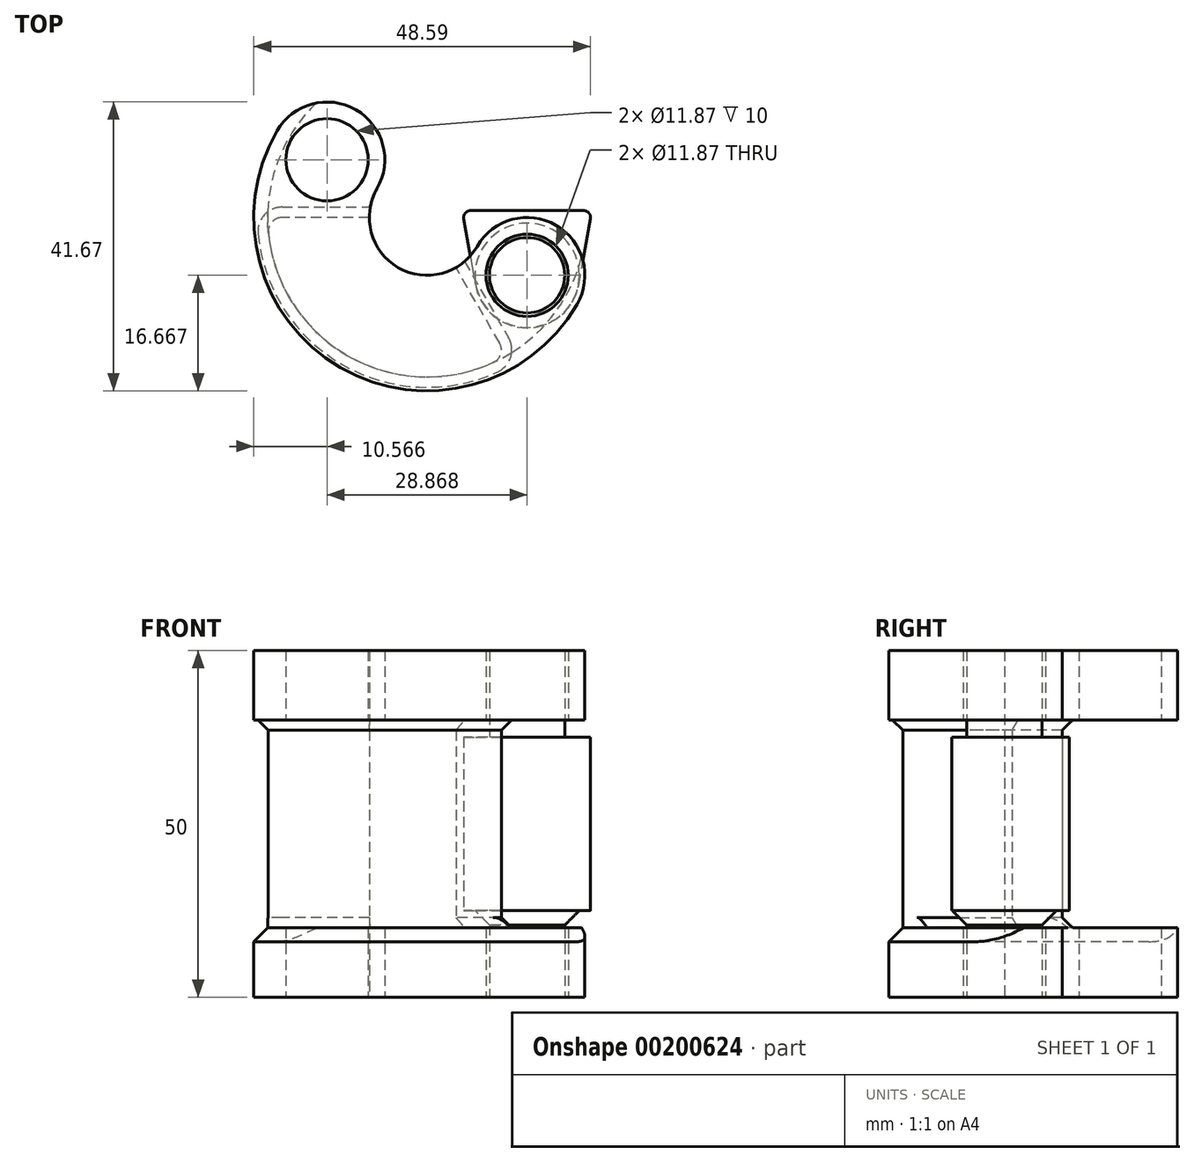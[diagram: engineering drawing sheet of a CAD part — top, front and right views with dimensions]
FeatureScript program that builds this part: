
annotation { "Feature Type Name" : "Feature", "Feature Type Description" : "" }
export const myFeature = defineFeature(function(context is Context, id is Id, definition is map)
    precondition{}
    {
        {
            assignVariable(context, id + "F0", {"name" : "height", "anyValue" : 50});
        }
        {
            var Q0;
            Q0=qCreatedBy(makeId("Top.planeOp"),FACE);
            var sketch = newSketch(context, id + "F1", { "sketchPlane" : qUnion([Q0])});
            skCircle(sketch, "E0", {"center": v(0, 0) * mm, "radius": 25 * mm});
            skLineSegment(sketch, "E1", {"start": v(25, 0) * mm, "end": v(0, 0) * mm});
            skLineSegment(sketch, "E2", {"start": v(0, 0) * mm, "end": v(-12.5, 21.65) * mm});
            skCircle(sketch, "E3", {"center": v(0, 0) * mm, "radius": 8.33 * mm});
            skCircle(sketch, "E4", {"center": v(0, 0) * mm, "radius": 23 * mm});
            skCircle(sketch, "E5", {"center": v(-14.43, 8.33) * mm, "radius": 8.33 * mm});
            skCircle(sketch, "E6", {"center": v(14.43, -8.33) * mm, "radius": 8.33 * mm});
            skCircle(sketch, "E7", {"center": v(-14.43, 8.33) * mm, "radius": 5.93 * mm});
            skCircle(sketch, "E8", {"center": v(14.43, -8.33) * mm, "radius": 5.93 * mm});
            skLineSegment(sketch, "E9", {"start": v(4.17, -7.22) * mm, "end": v(12.5, -21.65) * mm});
            skLineSegment(sketch, "E10", {"start": v(-8.33, 0) * mm, "end": v(-25, 0) * mm});
            skSolve(sketch);
        }
        {
            var Q0;
            {var subQ0=sQuery(id+"F1.wireOp",EDGE,"E5");var subQ1=sQuery(id+"F1.wireOp",EDGE,"E3");var subQ2=makeQuery(id+"F1.imprint","INTERSECT",VERTEX,{"derivedFrom":[subQ1,subQ0]});Q0=makeQuery(id+"F1.imprint","IMPRINT",FACE,{"disambiguationData":[TD([[makeQuery(id+"F1.imprint","IMPRINT",EDGE,{"disambiguationData":[TD([[subQ2,-1.0]])],"derivedFrom":subQ1}),-1.0]])]});}
            var Q1;
            {var subQ0=sQuery(id+"F1.wireOp",EDGE,"E5");var subQ1=sQuery(id+"F1.wireOp",EDGE,"E4");var subQ2=makeQuery(id+"F1.imprint","INTERSECT",VERTEX,{"disambiguationData":[OD(0.0)],"derivedFrom":[subQ1,subQ0]});Q1=makeQuery(id+"F1.imprint","IMPRINT",FACE,{"disambiguationData":[TD([[makeQuery(id+"F1.imprint","IMPRINT",EDGE,{"disambiguationData":[TD([[subQ2,-1.0]])],"derivedFrom":subQ1}),1.0]])]});}
            var Q2;
            {var subQ0=sQuery(id+"F1.wireOp",EDGE,"E6");var subQ1=sQuery(id+"F1.wireOp",EDGE,"E4");var subQ2=makeQuery(id+"F1.imprint","INTERSECT",VERTEX,{"disambiguationData":[OD(0.0)],"derivedFrom":[subQ1,subQ0]});Q2=makeQuery(id+"F1.imprint","IMPRINT",FACE,{"disambiguationData":[TD([[makeQuery(id+"F1.imprint","IMPRINT",EDGE,{"disambiguationData":[TD([[subQ2,-1.0]])],"derivedFrom":subQ1}),1.0]])]});}
            var Q3;
            {var subQ0=sQuery(id+"F1.wireOp",EDGE,"E5");var subQ1=sQuery(id+"F1.wireOp",EDGE,"E0");var subQ2=makeQuery(id+"F1.imprint","INTERSECT",VERTEX,{"derivedFrom":[subQ1,subQ0]});Q3=makeQuery(id+"F1.imprint","IMPRINT",FACE,{"disambiguationData":[TD([[makeQuery(id+"F1.imprint","IMPRINT",EDGE,{"disambiguationData":[TD([[subQ2,-1.0]])],"derivedFrom":subQ1}),1.0]])]});}
            var Q4;
            {var subQ0=sQuery(id+"F1.wireOp",EDGE,"E5");var subQ1=sQuery(id+"F1.wireOp",EDGE,"E4");var subQ2=makeQuery(id+"F1.imprint","INTERSECT",VERTEX,{"disambiguationData":[OD(0.0)],"derivedFrom":[subQ1,subQ0]});Q4=makeQuery(id+"F1.imprint","IMPRINT",FACE,{"disambiguationData":[TD([[makeQuery(id+"F1.imprint","IMPRINT",EDGE,{"disambiguationData":[TD([[subQ2,-1.0]])],"derivedFrom":subQ1}),-1.0]])]});}
            var Q5;
            {var subQ0=sQuery(id+"F1.wireOp",EDGE,"E6");var subQ1=sQuery(id+"F1.wireOp",EDGE,"E4");var subQ2=makeQuery(id+"F1.imprint","INTERSECT",VERTEX,{"disambiguationData":[OD(0.0)],"derivedFrom":[subQ1,subQ0]});Q5=makeQuery(id+"F1.imprint","IMPRINT",FACE,{"disambiguationData":[TD([[makeQuery(id+"F1.imprint","IMPRINT",EDGE,{"disambiguationData":[TD([[subQ2,-1.0]])],"derivedFrom":subQ1}),-1.0]])]});}
            var Q6;
            {var subQ0=sQuery(id+"F1.wireOp",EDGE,"E5");var subQ1=sQuery(id+"F1.wireOp",EDGE,"E4");var subQ2=makeQuery(id+"F1.imprint","INTERSECT",VERTEX,{"disambiguationData":[OD(1.0)],"derivedFrom":[subQ1,subQ0]});Q6=makeQuery(id+"F1.imprint","IMPRINT",FACE,{"disambiguationData":[TD([[makeQuery(id+"F1.imprint","IMPRINT",EDGE,{"disambiguationData":[TD([[subQ2,-1.0]])],"derivedFrom":subQ1}),1.0]])]});}
            var Q7;
            {var subQ0=sQuery(id+"F1.wireOp",EDGE,"E9");var subQ4=sQuery(id+"F1.wireOp",EDGE,"E3");var subQ5=makeQuery(id+"F1.imprint","INTERSECT",VERTEX,{"derivedFrom":[subQ4,subQ0]});Q7=makeQuery(id+"F1.imprint","IMPRINT",FACE,{"disambiguationData":[TD([[makeQuery(id+"F1.imprint","IMPRINT",EDGE,{"disambiguationData":[TD([[subQ5,1.0]])],"derivedFrom":subQ4}),-1.0]])]});}
            var Q8;
            {var subQ0=sQuery(id+"F1.wireOp",EDGE,"E9");var subQ1=sQuery(id+"F1.wireOp",EDGE,"E0");var subQ2=makeQuery(id+"F1.imprint","INTERSECT",VERTEX,{"derivedFrom":[subQ1,subQ0]});Q8=makeQuery(id+"F1.imprint","IMPRINT",FACE,{"disambiguationData":[TD([[makeQuery(id+"F1.imprint","IMPRINT",EDGE,{"disambiguationData":[TD([[subQ2,1.0]])],"derivedFrom":subQ1}),1.0]])]});}
            var Q9;
            {var subQ0=sQuery(id+"F1.wireOp",EDGE,"E9");var subQ1=sQuery(id+"F1.wireOp",EDGE,"E3");var subQ2=makeQuery(id+"F1.imprint","INTERSECT",VERTEX,{"derivedFrom":[subQ1,subQ0]});Q9=makeQuery(id+"F1.imprint","IMPRINT",FACE,{"disambiguationData":[TD([[makeQuery(id+"F1.imprint","IMPRINT",EDGE,{"disambiguationData":[TD([[subQ2,-1.0]])],"derivedFrom":subQ1}),-1.0]])]});}
            var Q10;
            {var subQ0=sQuery(id+"F1.wireOp",EDGE,"E9");var subQ1=sQuery(id+"F1.wireOp",EDGE,"E4");var subQ2=makeQuery(id+"F1.imprint","INTERSECT",VERTEX,{"derivedFrom":[subQ1,subQ0]});Q10=makeQuery(id+"F1.imprint","IMPRINT",FACE,{"disambiguationData":[TD([[makeQuery(id+"F1.imprint","IMPRINT",EDGE,{"disambiguationData":[TD([[subQ2,-1.0]])],"derivedFrom":subQ1}),1.0]])]});}
            var Q11;
            {var subQ0=sQuery(id+"F1.wireOp",EDGE,"E9");var subQ1=sQuery(id+"F1.wireOp",EDGE,"E0");var subQ2=makeQuery(id+"F1.imprint","INTERSECT",VERTEX,{"derivedFrom":[subQ1,subQ0]});Q11=makeQuery(id+"F1.imprint","IMPRINT",FACE,{"disambiguationData":[TD([[makeQuery(id+"F1.imprint","IMPRINT",EDGE,{"disambiguationData":[TD([[subQ2,-1.0]])],"derivedFrom":subQ1}),1.0]])]});}
            extrude(context, id + "F2", {"entities" : qUnion([Q0, Q1, Q2, Q3, Q4, Q5, Q6, Q7, Q8, Q9, Q10, Q11]), "endBound" : BoundingType.SYMMETRIC, "depth" : (getVariable(context, 'height')) * mm});
        }
        {
            var Q0;
            {var subQ0=sQuery(id+"F1.wireOp",EDGE,"E5");var subQ1=sQuery(id+"F1.wireOp",EDGE,"E0");var subQ2=makeQuery(id+"F1.imprint","INTERSECT",VERTEX,{"derivedFrom":[subQ1,subQ0]});Q0=makeQuery(id+"F1.imprint","IMPRINT",FACE,{"disambiguationData":[TD([[makeQuery(id+"F1.imprint","IMPRINT",EDGE,{"disambiguationData":[TD([[subQ2,-1.0]])],"derivedFrom":subQ1}),1.0]])]});}
            var Q1;
            {var subQ0=sQuery(id+"F1.wireOp",EDGE,"E5");var subQ1=sQuery(id+"F1.wireOp",EDGE,"E4");var subQ2=makeQuery(id+"F1.imprint","INTERSECT",VERTEX,{"disambiguationData":[OD(0.0)],"derivedFrom":[subQ1,subQ0]});Q1=makeQuery(id+"F1.imprint","IMPRINT",FACE,{"disambiguationData":[TD([[makeQuery(id+"F1.imprint","IMPRINT",EDGE,{"disambiguationData":[TD([[subQ2,-1.0]])],"derivedFrom":subQ1}),-1.0]])]});}
            var Q2;
            {var subQ0=sQuery(id+"F1.wireOp",EDGE,"E6");var subQ1=sQuery(id+"F1.wireOp",EDGE,"E4");var subQ2=makeQuery(id+"F1.imprint","INTERSECT",VERTEX,{"disambiguationData":[OD(0.0)],"derivedFrom":[subQ1,subQ0]});Q2=makeQuery(id+"F1.imprint","IMPRINT",FACE,{"disambiguationData":[TD([[makeQuery(id+"F1.imprint","IMPRINT",EDGE,{"disambiguationData":[TD([[subQ2,-1.0]])],"derivedFrom":subQ1}),-1.0]])]});}
            var Q3;
            {var subQ0=sQuery(id+"F1.wireOp",EDGE,"E9");var subQ1=sQuery(id+"F1.wireOp",EDGE,"E0");var subQ2=makeQuery(id+"F1.imprint","INTERSECT",VERTEX,{"derivedFrom":[subQ1,subQ0]});Q3=makeQuery(id+"F1.imprint","IMPRINT",FACE,{"disambiguationData":[TD([[makeQuery(id+"F1.imprint","IMPRINT",EDGE,{"disambiguationData":[TD([[subQ2,1.0]])],"derivedFrom":subQ1}),1.0]])]});}
            var Q4;
            {var subQ0=sQuery(id+"F1.wireOp",EDGE,"E9");var subQ1=sQuery(id+"F1.wireOp",EDGE,"E0");var subQ2=makeQuery(id+"F1.imprint","INTERSECT",VERTEX,{"derivedFrom":[subQ1,subQ0]});Q4=makeQuery(id+"F1.imprint","IMPRINT",FACE,{"disambiguationData":[TD([[makeQuery(id+"F1.imprint","IMPRINT",EDGE,{"disambiguationData":[TD([[subQ2,-1.0]])],"derivedFrom":subQ1}),1.0]])]});}
            extrude(context, id + "F3", {"entities" : qUnion([Q0, Q1, Q2, Q3, Q4]), "operationType" : NewBodyOperationType.REMOVE, "endBound" : BoundingType.SYMMETRIC, "oppositeDirection" : true, "depth" : 30 * mm});
        }
        {
            var Q0;
            Q0=makeQuery(id+"F1.imprint","IMPRINT",FACE,{"disambiguationData":[TD([[makeQuery(id+"F1.imprint","IMPRINT",EDGE,{"derivedFrom":sQuery(id+"F1.wireOp",EDGE,"E7")}),-1.0]])]});
            var Q1;
            Q1=makeQuery(id+"F1.imprint","IMPRINT",FACE,{"disambiguationData":[TD([[makeQuery(id+"F1.imprint","IMPRINT",EDGE,{"derivedFrom":sQuery(id+"F1.wireOp",EDGE,"E7")}),1.0]])]});
            var Q2;
            {var subQ0=sQuery(id+"F1.wireOp",EDGE,"E5");var subQ1=sQuery(id+"F1.wireOp",EDGE,"E4");var subQ2=makeQuery(id+"F1.imprint","INTERSECT",VERTEX,{"disambiguationData":[OD(0.0)],"derivedFrom":[subQ1,subQ0]});Q2=makeQuery(id+"F1.imprint","IMPRINT",FACE,{"disambiguationData":[TD([[makeQuery(id+"F1.imprint","IMPRINT",EDGE,{"disambiguationData":[TD([[subQ2,-1.0]])],"derivedFrom":subQ1}),-1.0]])]});}
            var Q3;
            Q3=makeQuery(id+"F1.imprint","IMPRINT",FACE,{"disambiguationData":[TD([[makeQuery(id+"F1.imprint","IMPRINT",EDGE,{"derivedFrom":sQuery(id+"F1.wireOp",EDGE,"E8")}),-1.0]])]});
            var Q4;
            Q4=makeQuery(id+"F1.imprint","IMPRINT",FACE,{"disambiguationData":[TD([[makeQuery(id+"F1.imprint","IMPRINT",EDGE,{"derivedFrom":sQuery(id+"F1.wireOp",EDGE,"E8")}),1.0]])]});
            var Q5;
            {var subQ0=sQuery(id+"F1.wireOp",EDGE,"E6");var subQ1=sQuery(id+"F1.wireOp",EDGE,"E4");var subQ2=makeQuery(id+"F1.imprint","INTERSECT",VERTEX,{"disambiguationData":[OD(0.0)],"derivedFrom":[subQ1,subQ0]});Q5=makeQuery(id+"F1.imprint","IMPRINT",FACE,{"disambiguationData":[TD([[makeQuery(id+"F1.imprint","IMPRINT",EDGE,{"disambiguationData":[TD([[subQ2,-1.0]])],"derivedFrom":subQ1}),-1.0]])]});}
            var Q6;
            {var subQ0=sQuery(id+"F1.wireOp",EDGE,"E9");var subQ1=sQuery(id+"F1.wireOp",EDGE,"E0");var subQ2=makeQuery(id+"F1.imprint","INTERSECT",VERTEX,{"derivedFrom":[subQ1,subQ0]});Q6=makeQuery(id+"F1.imprint","IMPRINT",FACE,{"disambiguationData":[TD([[makeQuery(id+"F1.imprint","IMPRINT",EDGE,{"disambiguationData":[TD([[subQ2,-1.0]])],"derivedFrom":subQ1}),1.0]])]});}
            var Q7;
            {var subQ0=sQuery(id+"F1.wireOp",EDGE,"E9");var subQ1=sQuery(id+"F1.wireOp",EDGE,"E4");var subQ2=makeQuery(id+"F1.imprint","INTERSECT",VERTEX,{"derivedFrom":[subQ1,subQ0]});Q7=makeQuery(id+"F1.imprint","IMPRINT",FACE,{"disambiguationData":[TD([[makeQuery(id+"F1.imprint","IMPRINT",EDGE,{"disambiguationData":[TD([[subQ2,-1.0]])],"derivedFrom":subQ1}),1.0]])]});}
            var Q8;
            {var subQ0=sQuery(id+"F1.wireOp",EDGE,"E9");var subQ1=sQuery(id+"F1.wireOp",EDGE,"E3");var subQ2=makeQuery(id+"F1.imprint","INTERSECT",VERTEX,{"derivedFrom":[subQ1,subQ0]});Q8=makeQuery(id+"F1.imprint","IMPRINT",FACE,{"disambiguationData":[TD([[makeQuery(id+"F1.imprint","IMPRINT",EDGE,{"disambiguationData":[TD([[subQ2,-1.0]])],"derivedFrom":subQ1}),-1.0]])]});}
            var Q9;
            {var subQ0=sQuery(id+"F1.wireOp",EDGE,"E10");var subQ1=sQuery(id+"F1.wireOp",EDGE,"E3");var subQ2=makeQuery(id+"F1.imprint","INTERSECT",VERTEX,{"derivedFrom":[subQ1,subQ0]});Q9=makeQuery(id+"F1.imprint","IMPRINT",FACE,{"disambiguationData":[TD([[makeQuery(id+"F1.imprint","IMPRINT",EDGE,{"disambiguationData":[TD([[subQ2,1.0]])],"derivedFrom":subQ1}),-1.0]])]});}
            var Q10;
            {var subQ0=sQuery(id+"F1.wireOp",EDGE,"E5");var subQ1=sQuery(id+"F1.wireOp",EDGE,"E4");var subQ2=makeQuery(id+"F1.imprint","INTERSECT",VERTEX,{"disambiguationData":[OD(1.0)],"derivedFrom":[subQ1,subQ0]});Q10=makeQuery(id+"F1.imprint","IMPRINT",FACE,{"disambiguationData":[TD([[makeQuery(id+"F1.imprint","IMPRINT",EDGE,{"disambiguationData":[TD([[subQ2,-1.0]])],"derivedFrom":subQ1}),1.0]])]});}
            var Q11;
            {var subQ0=sQuery(id+"F1.wireOp",EDGE,"E10");var subQ1=sQuery(id+"F1.wireOp",EDGE,"E0");var subQ2=makeQuery(id+"F1.imprint","INTERSECT",VERTEX,{"derivedFrom":[subQ1,subQ0]});Q11=makeQuery(id+"F1.imprint","IMPRINT",FACE,{"disambiguationData":[TD([[makeQuery(id+"F1.imprint","IMPRINT",EDGE,{"disambiguationData":[TD([[subQ2,1.0]])],"derivedFrom":subQ1}),1.0]])]});}
            extrude(context, id + "F4", {"entities" : qUnion([Q0, Q1, Q2, Q3, Q4, Q5, Q6, Q7, Q8, Q9, Q10, Q11]), "operationType" : NewBodyOperationType.REMOVE, "endBound" : BoundingType.SYMMETRIC, "depth" : 30 * mm});
        }
        {
            var Q0;
            Q0=makeQuery(id+"F3.boolean.opBoolean","COPY",EDGE,{"derivedFrom":makeQuery(id+"F3.opExtrude","CAP_EDGE",EDGE,{"disambiguationData":[OSD([sQuery(id+"F1.wireOp",EDGE,"E0")])],"isStart":true})});
            var Q1;
            Q1=makeQuery(id+"F3.boolean.opBoolean","COPY",EDGE,{"derivedFrom":makeQuery(id+"F3.opExtrude","CAP_EDGE",EDGE,{"disambiguationData":[OSD([sQuery(id+"F1.wireOp",EDGE,"E0")])],"isStart":false})});
            chamfer(context, id + "F5", {"entities" : qUnion([Q0, Q1]), "width" : 2 * mm});
        }
        {
            var Q0;
            Q0=makeQuery(id+"F4.boolean.opBoolean","INTERSECT",EDGE,{"derivedFrom":[makeQuery(id+"F3.boolean.opBoolean","COPY",FACE,{"derivedFrom":makeQuery(id+"F3.opExtrude","SWEPT_FACE",FACE,{"disambiguationData":[OSD([sQuery(id+"F1.wireOp",EDGE,"E4")])]})}),makeQuery(id+"F4.opExtrude","SWEPT_FACE",FACE,{"disambiguationData":[OSD([sQuery(id+"F1.wireOp",EDGE,"E9")])]})]});
            var Q1;
            Q1=makeQuery(id+"F4.boolean.opBoolean","INTERSECT",EDGE,{"derivedFrom":[makeQuery(id+"F3.boolean.opBoolean","COPY",FACE,{"derivedFrom":makeQuery(id+"F3.opExtrude","SWEPT_FACE",FACE,{"disambiguationData":[OSD([sQuery(id+"F1.wireOp",EDGE,"E4")])]})}),makeQuery(id+"F4.opExtrude","SWEPT_FACE",FACE,{"disambiguationData":[OSD([sQuery(id+"F1.wireOp",EDGE,"E10")])]})]});
            var Q2;
            Q2=makeQuery(id+"F4.boolean.opBoolean","INTERSECT",EDGE,{"derivedFrom":[makeQuery(id+"F3.boolean.opBoolean","COPY",FACE,{"derivedFrom":makeQuery(id+"F3.opExtrude","SWEPT_FACE",FACE,{"disambiguationData":[OSD([sQuery(id+"F1.wireOp",EDGE,"E4")])]})}),makeQuery(id+"F4.opExtrude","SWEPT_FACE",FACE,{"disambiguationData":[OSD([sQuery(id+"F1.wireOp",EDGE,"E9")])]})]});
            var Q3;
            Q3=makeQuery(id+"F4.boolean.opBoolean","INTERSECT",EDGE,{"derivedFrom":[makeQuery(id+"F3.boolean.opBoolean","COPY",FACE,{"derivedFrom":makeQuery(id+"F3.opExtrude","SWEPT_FACE",FACE,{"disambiguationData":[OSD([sQuery(id+"F1.wireOp",EDGE,"E4")])]})}),makeQuery(id+"F4.opExtrude","SWEPT_FACE",FACE,{"disambiguationData":[OSD([sQuery(id+"F1.wireOp",EDGE,"E10")])]})]});
            var Q4;
            Q4=makeQuery(id+"F4.boolean.opBoolean","COPY",EDGE,{"derivedFrom":makeQuery(id+"F4.opExtrude","SWEPT_EDGE",EDGE,{"disambiguationData":[OSD([sQuery(id+"F1.wireOp",EDGE,"E3"),sQuery(id+"F1.wireOp",EDGE,"E9")])]})});
            var Q5;
            Q5=makeQuery(id+"F4.boolean.opBoolean","COPY",EDGE,{"derivedFrom":makeQuery(id+"F4.opExtrude","SWEPT_EDGE",EDGE,{"disambiguationData":[OSD([sQuery(id+"F1.wireOp",EDGE,"E3"),sQuery(id+"F1.wireOp",EDGE,"E10")])]})});
            fillet(context, id + "F6", {"entities" : qUnion([Q0, Q1, Q2, Q3, Q4, Q5]), "radius" : 2 * mm, "tangentPropagation" : true, "allowEdgeOverflow" : false});
        }
        {
            var Q0;
            Q0=makeQuery(id+"F4.boolean.opBoolean","COPY",EDGE,{"derivedFrom":makeQuery(id+"F4.opExtrude","CAP_EDGE",EDGE,{"disambiguationData":[OSD([sQuery(id+"F1.wireOp",EDGE,"E9")])],"isStart":false})});
            var Q1;
            Q1=makeQuery(id+"F4.boolean.opBoolean","COPY",EDGE,{"derivedFrom":makeQuery(id+"F4.opExtrude","CAP_EDGE",EDGE,{"disambiguationData":[OSD([sQuery(id+"F1.wireOp",EDGE,"E10")])],"isStart":false})});
            var Q2;
            Q2=makeQuery(id+"F4.boolean.opBoolean","COPY",EDGE,{"derivedFrom":makeQuery(id+"F4.opExtrude","CAP_EDGE",EDGE,{"disambiguationData":[OSD([sQuery(id+"F1.wireOp",EDGE,"E10")])],"isStart":true})});
            var Q3;
            Q3=makeQuery(id+"F4.boolean.opBoolean","COPY",EDGE,{"derivedFrom":makeQuery(id+"F4.opExtrude","CAP_EDGE",EDGE,{"disambiguationData":[OSD([sQuery(id+"F1.wireOp",EDGE,"E9")])],"isStart":true})});
            chamfer(context, id + "F7", {"entities" : qUnion([Q0, Q1, Q2, Q3]), "width" : 1.5 * mm, "tangentPropagation" : true});
        }
        {
            var Q0;
            Q0=qCreatedBy(makeId("Top.planeOp"),FACE);
            var sketch = newSketch(context, id + "F8", { "sketchPlane" : qUnion([Q0])});
            skCircle(sketch, "E11.0", {"center": v(14.43, -8.33) * mm, "radius": 5.93 * mm, "construction": true});
            skCircle(sketch, "E12", {"center": v(14.43, -8.33) * mm, "radius": 5.43 * mm});
            skCircle(sketch, "E13.0", {"center": v(14.43, -8.33) * mm, "radius": 8.33 * mm, "construction": true});
            skCircle(sketch, "E14", {"center": v(14.43, -8.33) * mm, "radius": 7.58 * mm});
            skLineSegment(sketch, "E15", {"start": v(21.9, -9.65) * mm, "end": v(23.78, 1) * mm});
            skLineSegment(sketch, "E16", {"start": v(23.78, 1) * mm, "end": v(5.09, 1) * mm});
            skLineSegment(sketch, "E17", {"start": v(5.09, 1) * mm, "end": v(6.97, -9.65) * mm});
            skSolve(sketch);
        }
        {
            var Q0;
            Q0=makeQuery(id+"F8.imprint","IMPRINT",FACE,{"disambiguationData":[TD([[makeQuery(id+"F8.imprint","IMPRINT",EDGE,{"derivedFrom":sQuery(id+"F8.wireOp",EDGE,"E12")}),1.0]])]});
            extrude(context, id + "F9", {"entities" : qUnion([Q0]), "endBound" : BoundingType.SYMMETRIC, "depth" : (getVariable(context, 'height')) * mm});
        }
        {
            var Q0;
            Q0=makeQuery(id+"F8.imprint","IMPRINT",FACE,{"disambiguationData":[TD([[makeQuery(id+"F8.imprint","IMPRINT",EDGE,{"derivedFrom":sQuery(id+"F8.wireOp",EDGE,"E12")}),-1.0]])]});
            var Q1;
            {var subQ0=sQuery(id+"F8.wireOp",EDGE,"E15");Q1=makeQuery(id+"F8.imprint","IMPRINT",FACE,{"disambiguationData":[TD([[makeQuery(id+"F8.imprint","IMPRINT",EDGE,{"derivedFrom":subQ0}),1.0]])]});}
            extrude(context, id + "F10", {"entities" : qUnion([Q0, Q1]), "operationType" : NewBodyOperationType.ADD, "endBound" : BoundingType.SYMMETRIC, "depth" : 25 * mm});
        }
        {
            var Q0;
            Q0=makeQuery(id+"F10.opExtrude","CAP_EDGE",EDGE,{"disambiguationData":[OSD([sQuery(id+"F8.wireOp",EDGE,"E12")])],"isStart":false});
            var Q1;
            Q1=makeQuery(id+"F10.opExtrude","CAP_EDGE",EDGE,{"disambiguationData":[OSD([sQuery(id+"F8.wireOp",EDGE,"E12")])],"isStart":true});
            chamfer(context, id + "F11", {"entities" : qUnion([Q0, Q1]), "width" : 2.1 * mm, "tangentPropagation" : true});
        }
        {
            var Q0;
            Q0=makeQuery(id+"F10.opExtrude","SWEPT_EDGE",EDGE,{"disambiguationData":[OSD([sQuery(id+"F8.wireOp",EDGE,"E16"),sQuery(id+"F8.wireOp",EDGE,"E17")])]});
            var Q1;
            Q1=makeQuery(id+"F10.opExtrude","SWEPT_EDGE",EDGE,{"disambiguationData":[OSD([sQuery(id+"F8.wireOp",EDGE,"E15"),sQuery(id+"F8.wireOp",EDGE,"E16")])]});
            fillet(context, id + "F12", {"entities" : qUnion([Q0, Q1]), "radius" : 1 * mm, "tangentPropagation" : true, "allowEdgeOverflow" : false});
        }
    });
